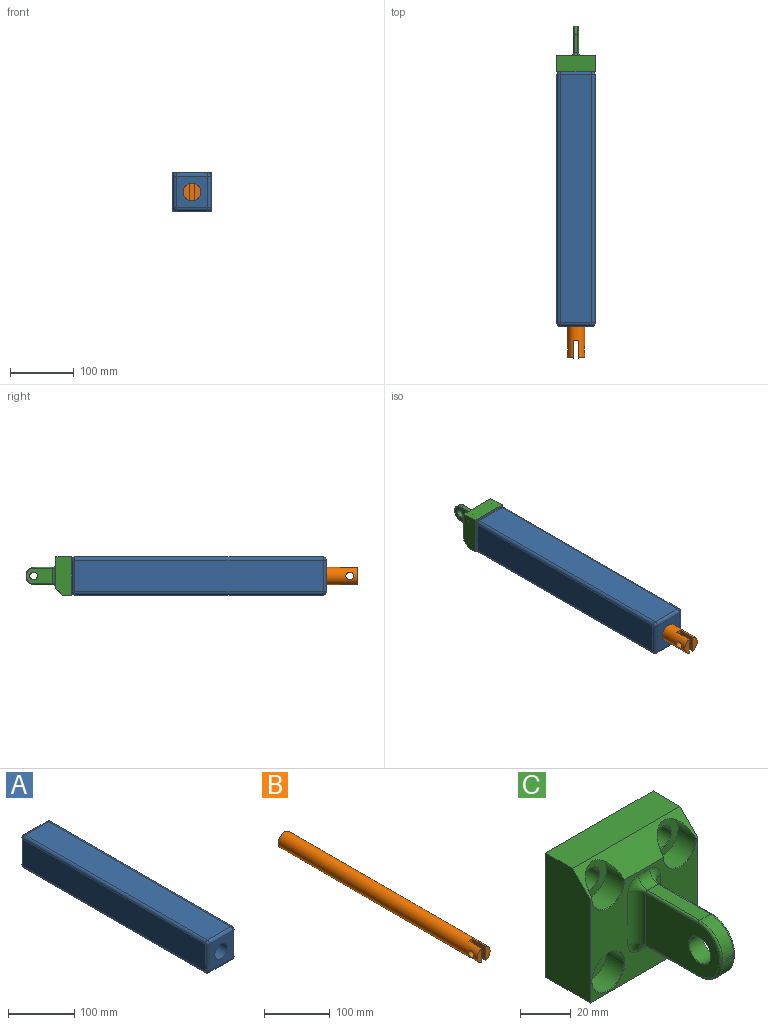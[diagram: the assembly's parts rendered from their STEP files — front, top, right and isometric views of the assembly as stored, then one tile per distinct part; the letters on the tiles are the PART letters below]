
ASSEMBLY  parts=3 mates=1
PART A: 28 faces, bbox 60x400x60 mm
  f0: plane 390x50mm, normal (0,0,1), area 19500mm2, adj f14,f19,f22,f25
  f1: plane 390x50mm, normal (-1,0,0), area 19500mm2, adj f11,f20,f21,f25
  f2: plane 390x50mm, normal (0,0,-1), area 19500mm2, adj f6,f10,f11,f12
  f3: plane 390x50mm, normal (1,0,0), area 19500mm2, adj f6,f9,f13,f14
  f4: plane 50x50mm, normal (0,-1,0), area 1884.2mm2, adj f9,f10,f19,f20,f26
  f5: plane 50x50mm, normal (0,1,0), area 2500mm2, adj f12,f13,f21,f22
  f6: cylinder r=5mm len=390mm, axis (0,-1,0), area 3063.1mm2, adj f2,f3,f7,f8
  f7: sphere r=5mm, area 39.3mm2, adj f6,f9,f10
  f8: sphere r=5mm, area 39.3mm2, adj f6,f12,f13
  f9: cylinder r=5mm len=50mm, axis (0,0,-1), area 392.7mm2, adj f3,f4,f7,f15
  f10: cylinder r=5mm len=50mm, axis (-1,0,0), area 392.7mm2, adj f2,f4,f7,f16
  f11: cylinder r=5mm len=390mm, axis (0,1,0), area 3063.1mm2, adj f1,f2,f16,f17
  f12: cylinder r=5mm len=50mm, axis (1,0,0), area 392.7mm2, adj f2,f5,f8,f17
  f13: cylinder r=5mm len=50mm, axis (0,0,1), area 392.7mm2, adj f3,f5,f8,f18
  f14: cylinder r=5mm len=390mm, axis (0,1,0), area 3063.1mm2, adj f0,f3,f15,f18
  f15: sphere r=5mm, area 39.3mm2, adj f9,f14,f19
  f16: sphere r=5mm, area 39.3mm2, adj f10,f11,f20
  f17: sphere r=5mm, area 39.3mm2, adj f11,f12,f21
  f18: sphere r=5mm, area 39.3mm2, adj f13,f14,f22
  f19: cylinder r=5mm len=50mm, axis (1,0,0), area 392.7mm2, adj f0,f4,f15,f23
  f20: cylinder r=5mm len=50mm, axis (0,0,1), area 392.7mm2, adj f1,f4,f16,f23
  f21: cylinder r=5mm len=50mm, axis (0,0,-1), area 392.7mm2, adj f1,f5,f17,f24
  f22: cylinder r=5mm len=50mm, axis (-1,0,0), area 392.7mm2, adj f0,f5,f18,f24
  f23: sphere r=5mm, area 39.3mm2, adj f19,f20,f25
  f24: sphere r=5mm, area 39.3mm2, adj f21,f22,f25
  f25: cylinder r=5mm len=390mm, axis (0,-1,0), area 3063.1mm2, adj f0,f1,f23,f24
  f26: cylinder r=14mm len=380mm, axis (0,-1,0), area 33426.5mm2, adj f4,f27
  f27: plane 28x28mm, normal (0,-1,0), area 615.8mm2, adj f26
PART B: 12 faces, bbox 27.8x430x27.8 mm
  f0: plane 26.56x9.76mm, normal (0,-1,0), area 191.1mm2, adj f2,f6,f10
  f1: cylinder r=6.1mm len=12.2mm, axis (1,0,0), area 348.8mm2, adj f2,f3,f6,f10
  f2: cylinder r=13.9mm len=430mm, axis (0,1,0), area 36810.5mm2, adj f0,f1,f3,f4,f5,f6,f7,f8
  f3: plane 15.99x2.04mm, normal (1,0,0), area 32.5mm2, adj f1,f2,f7
  f4: plane 26.56x9.8mm, normal (0,-1,0), area 191.2mm2, adj f2,f9
  f5: plane 27.8x27.8mm, normal (0,1,0), area 607mm2, adj f2
  f6: plane 6.99x2.04mm, normal (1,0,0), area 14.1mm2, adj f0,f1,f2
  f7: plane 2.04x0.04mm, normal (0,-1,0), area 0.1mm2, adj f2,f3
  f8: cylinder r=6.1mm len=12.2mm, axis (1,0,0), area 349mm2, adj f2,f9
  f9: plane 27.5x26.56mm, normal (1,0,0), area 613.6mm2, adj f2,f4,f8,f11
  f10: plane 27.5x26.56mm, normal (-1,0,0), area 613.6mm2, adj f0,f1,f2,f11
  f11: plane 27.8x8.2mm, normal (0,-1,0), area 224.6mm2, adj f2,f9,f10
PART C: 59 faces, bbox 60x73.1x60 mm
  f0: plane 60x50mm, normal (0,-1,0), area 1567.2mm2, adj f2,f3,f4,f28,f29,f30,f31,f50
  f1: plane 60x15mm, normal (0,0,1), area 900mm2, adj f2,f4,f5,f58
  f2: plane 60x25mm, normal (-1,0,0), area 1450mm2, adj f0,f1,f3,f5,f58
  f3: plane 60x25mm, normal (0,0,-1), area 1500mm2, adj f0,f2,f4,f5
  f4: plane 60x25mm, normal (1,0,0), area 1450mm2, adj f0,f1,f3,f5,f58
  f5: plane 60x60mm, normal (0,1,0), area 3260.2mm2, adj f1,f2,f3,f4,f33,f35,f37,f39
  f6: cylinder r=5mm len=14.6mm, axis (0,-1,0), area 458.7mm2, adj f36,f37
  f7: plane 18x18mm, normal (0,-1,0), area 169.5mm2, adj f8,f36
  f8: cylinder r=9mm len=18mm, axis (0,-1,0), area 397.8mm2, adj f7,f29,f58
  f9: cylinder r=5mm len=14.6mm, axis (0,-1,0), area 458.7mm2, adj f34,f35
  f10: plane 18x18mm, normal (0,-1,0), area 169.5mm2, adj f11,f34
  f11: cylinder r=9mm len=18mm, axis (0,-1,0), area 397.8mm2, adj f10,f30,f58
  f12: cylinder r=5mm len=14.6mm, axis (0,-1,0), area 458.7mm2, adj f32,f33
  f13: plane 18x18mm, normal (0,-1,0), area 169.5mm2, adj f14,f32
  f14: cylinder r=9mm len=18mm, axis (0,-1,0), area 554.2mm2, adj f13,f31
  f15: cylinder r=5mm len=14.6mm, axis (0,-1,0), area 458.7mm2, adj f38,f39
  f16: plane 18x18mm, normal (0,-1,0), area 169.5mm2, adj f17,f38
  f17: cylinder r=9mm len=18mm, axis (0,-1,0), area 554.2mm2, adj f16,f28
  f18: plane 29x6mm, normal (0,0,1), area 174mm2, adj f25,f40,f45,f53
  f19: plane 41x25mm, normal (-1,0,0), area 842.4mm2, adj f27,f40,f41,f42,f43,f44,f50
  f20: plane 29x6mm, normal (0,0,-1), area 174mm2, adj f24,f44,f49,f54
  f21: plane 41x25mm, normal (1,0,0), area 842.4mm2, adj f26,f45,f46,f47,f48,f49,f57
  f22: plane 6x1mm, normal (0,-1,0), area 6mm2, adj f24,f25,f42,f47
  f23: cylinder r=6mm len=12mm, axis (1,0,0), area 286.5mm2, adj f26,f27
  f24: cylinder r=13mm len=13mm, axis (-1,0,0), area 122.5mm2, adj f20,f22,f43,f48
  f25: cylinder r=13mm len=13mm, axis (1,0,0), area 122.5mm2, adj f18,f22,f41,f46
  f26: cone r=6.2mm half-angle=45deg, axis (1,0,0), area 10.8mm2, adj f21,f23
  f27: cone r=6mm half-angle=45deg, axis (-1,0,0), area 10.8mm2, adj f19,f23
  f28: cone r=9mm half-angle=45deg, axis (0,-1,0), area 16.2mm2, adj f0,f17
  f29: cone r=9mm half-angle=45deg, axis (0,-1,0), area 8.1mm2, adj f0,f8,f58
  f30: cone r=9mm half-angle=45deg, axis (0,-1,0), area 8.1mm2, adj f0,f11,f58
  f31: cone r=9mm half-angle=45deg, axis (0,-1,0), area 16.2mm2, adj f0,f14
  f32: cone r=5mm half-angle=45deg, axis (0,-1,0), area 9.1mm2, adj f12,f13
  f33: cone r=5mm half-angle=45deg, axis (0,1,0), area 9.1mm2, adj f5,f12
  f34: cone r=5mm half-angle=45deg, axis (0,-1,0), area 9.1mm2, adj f9,f10
  f35: cone r=5mm half-angle=45deg, axis (0,1,0), area 9.1mm2, adj f5,f9
  f36: cone r=5mm half-angle=45deg, axis (0,-1,0), area 9.1mm2, adj f6,f7
  f37: cone r=5mm half-angle=45deg, axis (0,1,0), area 9.1mm2, adj f5,f6
  f38: cone r=5mm half-angle=45deg, axis (0,-1,0), area 9.1mm2, adj f15,f16
  f39: cone r=5mm half-angle=45deg, axis (0,1,0), area 9.1mm2, adj f5,f15
  f40: cylinder r=1mm len=29mm, axis (0,-1,0), area 45.6mm2, adj f18,f19,f41,f51
  f41: torus R=12mm, axis (1,0,0), area 31.2mm2, adj f19,f25,f40,f42
  f42: cylinder r=1mm len=1mm, axis (0,0,1), area 1.6mm2, adj f19,f22,f41,f43
  f43: torus R=12mm, axis (1,0,0), area 31.2mm2, adj f19,f24,f42,f44
  f44: cylinder r=1mm len=29mm, axis (0,1,0), area 45.6mm2, adj f19,f20,f43,f52
  f45: cylinder r=1mm len=29mm, axis (0,1,0), area 45.6mm2, adj f18,f21,f46,f55
  f46: torus R=12mm, axis (1,0,0), area 31.2mm2, adj f21,f25,f45,f47
  f47: cylinder r=1mm len=1mm, axis (0,0,-1), area 1.6mm2, adj f21,f22,f46,f48
  f48: torus R=12mm, axis (1,0,0), area 31.2mm2, adj f21,f24,f47,f49
  f49: cylinder r=1mm len=29mm, axis (0,-1,0), area 45.6mm2, adj f20,f21,f48,f56
  f50: cylinder r=5mm len=25mm, axis (0,0,-1), area 196.3mm2, adj f0,f19,f51,f52
  f51: torus R=6mm, axis (0,-1,0), area 34.8mm2, adj f0,f40,f50,f53
  f52: torus R=6mm, axis (0,-1,0), area 34.8mm2, adj f0,f44,f50,f54
  f53: cylinder r=5mm len=6mm, axis (-1,0,0), area 47.1mm2, adj f0,f18,f51,f55
  f54: cylinder r=5mm len=6mm, axis (1,0,0), area 47.1mm2, adj f0,f20,f52,f56
  f55: torus R=6mm, axis (0,-1,0), area 34.8mm2, adj f0,f45,f53,f57
  f56: torus R=6mm, axis (0,-1,0), area 34.8mm2, adj f0,f49,f54,f57
  f57: cylinder r=5mm len=25mm, axis (0,0,1), area 196.3mm2, adj f0,f21,f55,f56
  f58: plane 60x10mm, normal (0,-0.71,0.71), area 488.5mm2, adj f0,f1,f2,f4,f8,f11,f29,f30
PLACE A t=(-49.33,-26.45,3.04)mm fixed
PLACE B t=(-49.33,-61.45,3.04)mm
PLACE C rot(axis=(1,0,0),180deg) t=(-49.33,186.05,3.04)mm
MATE slider B.f2 <-> A.f26  axis (0,1,0) through (-49.33,153.55,3.04)mm
